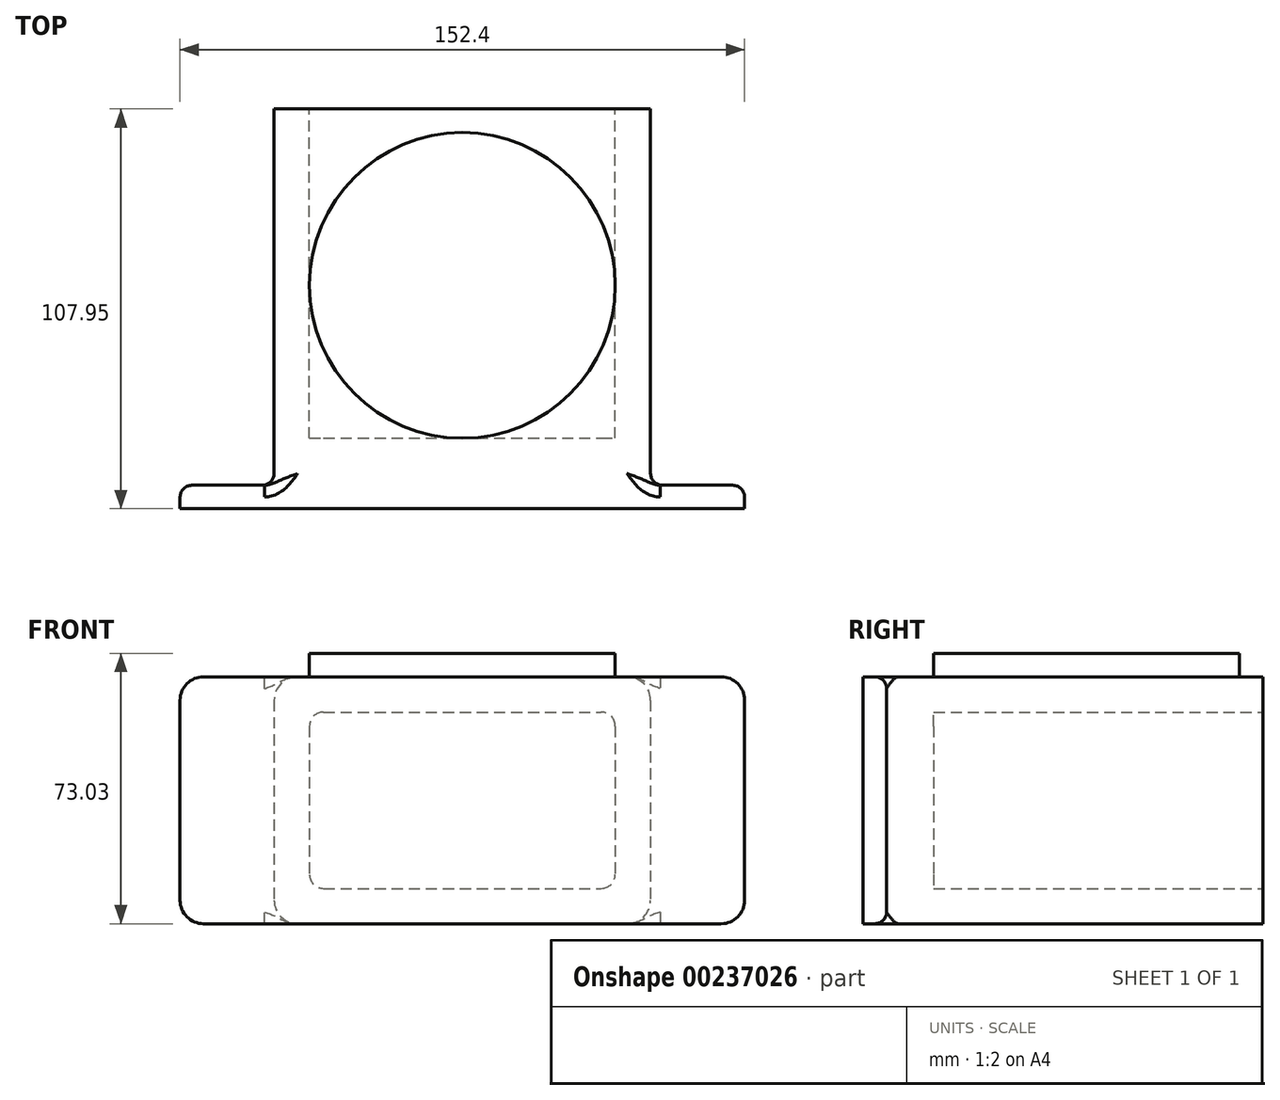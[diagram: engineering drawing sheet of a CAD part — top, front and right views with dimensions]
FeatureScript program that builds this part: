
annotation { "Feature Type Name" : "Feature", "Feature Type Description" : "" }
export const myFeature = defineFeature(function(context is Context, id is Id, definition is map)
    precondition{}
    {
        {
            var Q0;
            Q0=qCreatedBy(makeId("Front.planeOp"),FACE);
            var sketch = newSketch(context, id + "F0", { "sketchPlane" : qUnion([Q0])});
            skLineSegment(sketch, "E0.bottom", {"start": v(-76.2, -33.34) * mm, "end": v(76.2, -33.34) * mm});
            skLineSegment(sketch, "E0.top", {"start": v(-76.2, 33.34) * mm, "end": v(76.2, 33.34) * mm});
            skLineSegment(sketch, "E0.left", {"start": v(-76.2, -33.34) * mm, "end": v(-76.2, 33.34) * mm});
            skLineSegment(sketch, "E0.right", {"start": v(76.2, -33.34) * mm, "end": v(76.2, 33.34) * mm});
            skPoint(sketch, "E0.middle", {"position": v(0, 0) * mm});
            skSolve(sketch);
        }
        {
            var Q0;
            Q0=makeQuery(id+"F0.imprint","IMPRINT",FACE,{"disambiguationData":[TD([[makeQuery(id+"F0.imprint","IMPRINT",EDGE,{"derivedFrom":sQuery(id+"F0.wireOp",EDGE,"E0.bottom")}),1.0]])]});
            extrude(context, id + "F1", {"entities" : qUnion([Q0]), "depth" : 6.35 * mm});
        }
        {
            var Q0;
            Q0=makeQuery(id+"F1.opExtrude","CAP_FACE",FACE,{"disambiguationData":[OSD([sQuery(id+"F0.wireOp",EDGE,"E0.bottom"),sQuery(id+"F0.wireOp",EDGE,"E0.top"),sQuery(id+"F0.wireOp",EDGE,"E0.left"),sQuery(id+"F0.wireOp",EDGE,"E0.right")])],"isStart":true});
            var sketch = newSketch(context, id + "F2", { "sketchPlane" : qUnion([Q0])});
            skLineSegment(sketch, "E1.bottom", {"start": v(50.8, 33.34) * mm, "end": v(-50.8, 33.34) * mm});
            skLineSegment(sketch, "E1.top", {"start": v(50.8, -33.34) * mm, "end": v(-50.8, -33.34) * mm});
            skLineSegment(sketch, "E1.left", {"start": v(50.8, 33.34) * mm, "end": v(50.8, -33.34) * mm});
            skLineSegment(sketch, "E1.right", {"start": v(-50.8, 33.34) * mm, "end": v(-50.8, -33.34) * mm});
            skPoint(sketch, "E1.middle", {"position": v(0, 0) * mm});
            skSolve(sketch);
        }
        {
            var Q0;
            Q0=makeQuery(id+"F2.imprint","IMPRINT",FACE,{"disambiguationData":[TD([[makeQuery(id+"F2.imprint","IMPRINT",EDGE,{"derivedFrom":sQuery(id+"F2.wireOp",EDGE,"E1.bottom")}),1.0]])]});
            extrude(context, id + "F3", {"entities" : qUnion([Q0]), "operationType" : NewBodyOperationType.ADD, "depth" : 101.6 * mm});
        }
        {
            var Q0;
            Q0=makeQuery(id+"F3.opExtrude","SWEPT_EDGE",EDGE,{"disambiguationData":[OSD([sQuery(id+"F0.wireOp",EDGE,"E0.bottom"),sQuery(id+"F2.wireOp",EDGE,"E1.top"),sQuery(id+"F2.wireOp",EDGE,"E1.right")])]});
            var Q1;
            Q1=makeQuery(id+"F3.opExtrude","SWEPT_EDGE",EDGE,{"disambiguationData":[OSD([sQuery(id+"F0.wireOp",EDGE,"E0.top"),sQuery(id+"F2.wireOp",EDGE,"E1.bottom"),sQuery(id+"F2.wireOp",EDGE,"E1.right")])]});
            var Q2;
            Q2=makeQuery(id+"F3.opExtrude","SWEPT_EDGE",EDGE,{"disambiguationData":[OSD([sQuery(id+"F0.wireOp",EDGE,"E0.bottom"),sQuery(id+"F2.wireOp",EDGE,"E1.top"),sQuery(id+"F2.wireOp",EDGE,"E1.left")])]});
            var Q3;
            Q3=makeQuery(id+"F3.opExtrude","SWEPT_EDGE",EDGE,{"disambiguationData":[OSD([sQuery(id+"F0.wireOp",EDGE,"E0.top"),sQuery(id+"F2.wireOp",EDGE,"E1.bottom"),sQuery(id+"F2.wireOp",EDGE,"E1.left")])]});
            var Q4;
            Q4=makeQuery(id+"F1.opExtrude","SWEPT_EDGE",EDGE,{"disambiguationData":[OSD([sQuery(id+"F0.wireOp",EDGE,"E0.bottom"),sQuery(id+"F0.wireOp",EDGE,"E0.left")])]});
            var Q5;
            Q5=makeQuery(id+"F1.opExtrude","SWEPT_EDGE",EDGE,{"disambiguationData":[OSD([sQuery(id+"F0.wireOp",EDGE,"E0.top"),sQuery(id+"F0.wireOp",EDGE,"E0.left")])]});
            var Q6;
            Q6=makeQuery(id+"F1.opExtrude","SWEPT_EDGE",EDGE,{"disambiguationData":[OSD([sQuery(id+"F0.wireOp",EDGE,"E0.top"),sQuery(id+"F0.wireOp",EDGE,"E0.right")])]});
            var Q7;
            Q7=makeQuery(id+"F1.opExtrude","SWEPT_EDGE",EDGE,{"disambiguationData":[OSD([sQuery(id+"F0.wireOp",EDGE,"E0.bottom"),sQuery(id+"F0.wireOp",EDGE,"E0.right")])]});
            fillet(context, id + "F4", {"entities" : qUnion([Q0, Q1, Q2, Q3, Q4, Q5, Q6, Q7]), "radius" : 6.35 * mm, "tangentPropagation" : true, "allowEdgeOverflow" : false});
        }
        {
            var Q0;
            {var subQ0=sQuery(id+"F0.wireOp",EDGE,"E0.left");var subQ1=sQuery(id+"F0.wireOp",EDGE,"E0.top");var subQ2=sQuery(id+"F0.wireOp",EDGE,"E0.bottom");Q0=makeQuery(id+"F3.boolean.opBoolean","SPLIT",FACE,{"disambiguationData":[TD([makeQuery(id+"F1.opExtrude","SWEPT_FACE",FACE,{"disambiguationData":[OSD([subQ0])]})])],"derivedFrom":makeQuery(id+"F1.opExtrude","CAP_FACE",FACE,{"disambiguationData":[OSD([subQ2,subQ1,subQ0,sQuery(id+"F0.wireOp",EDGE,"E0.right")])],"isStart":true})});}
            var Q1;
            {var subQ0=sQuery(id+"F0.wireOp",EDGE,"E0.right");var subQ1=sQuery(id+"F0.wireOp",EDGE,"E0.top");var subQ2=sQuery(id+"F0.wireOp",EDGE,"E0.bottom");Q1=makeQuery(id+"F3.boolean.opBoolean","SPLIT",FACE,{"disambiguationData":[TD([makeQuery(id+"F1.opExtrude","SWEPT_FACE",FACE,{"disambiguationData":[OSD([subQ0])]})])],"derivedFrom":makeQuery(id+"F1.opExtrude","CAP_FACE",FACE,{"disambiguationData":[OSD([subQ2,subQ1,sQuery(id+"F0.wireOp",EDGE,"E0.left"),subQ0])],"isStart":true})});}
            fillet(context, id + "F5", {"entities" : qUnion([Q0, Q1]), "radius" : 3.17 * mm, "tangentPropagation" : true, "allowEdgeOverflow" : false});
        }
        {
            var Q0;
            Q0=makeQuery(id+"F3.opExtrude","CAP_FACE",FACE,{"disambiguationData":[OSD([sQuery(id+"F2.wireOp",EDGE,"E1.bottom"),sQuery(id+"F2.wireOp",EDGE,"E1.top"),sQuery(id+"F2.wireOp",EDGE,"E1.left"),sQuery(id+"F2.wireOp",EDGE,"E1.right")])],"isStart":false});
            var sketch = newSketch(context, id + "F6", { "sketchPlane" : qUnion([Q0])});
            skLineSegment(sketch, "E2.bottom", {"start": v(37.47, 23.81) * mm, "end": v(-37.46, 23.81) * mm});
            skLineSegment(sketch, "E2.top", {"start": v(37.47, -23.81) * mm, "end": v(-37.46, -23.81) * mm});
            skLineSegment(sketch, "E2.left", {"start": v(41.28, 20) * mm, "end": v(41.28, -20) * mm});
            skLineSegment(sketch, "E2.right", {"start": v(-41.27, 20) * mm, "end": v(-41.27, -20) * mm});
            skPoint(sketch, "E2.middle", {"position": v(0, 0) * mm});
            skPoint(sketch, "E3.visualSharp", {"position": v(-41.28, 23.81) * mm});
            skArc(sketch, "E3.filletArc", {"start": v(-37.46, 23.81) * mm, "mid": v(-40.16, 22.7) * mm, "end": v(-41.28, 20) * mm});
            skPoint(sketch, "E4.visualSharp", {"position": v(41.27, 23.81) * mm});
            skArc(sketch, "E4.filletArc", {"start": v(41.28, 20) * mm, "mid": v(40.16, 22.7) * mm, "end": v(37.47, 23.81) * mm});
            skPoint(sketch, "E5.visualSharp", {"position": v(41.27, -23.81) * mm});
            skArc(sketch, "E5.filletArc", {"start": v(37.47, -23.81) * mm, "mid": v(40.16, -22.7) * mm, "end": v(41.28, -20) * mm});
            skPoint(sketch, "E6.visualSharp", {"position": v(-41.28, -23.81) * mm});
            skArc(sketch, "E6.filletArc", {"start": v(-41.28, -20) * mm, "mid": v(-40.16, -22.7) * mm, "end": v(-37.46, -23.81) * mm});
            skSolve(sketch);
        }
        {
            var Q0;
            Q0=makeQuery(id+"F6.imprint","IMPRINT",FACE,{"disambiguationData":[TD([[makeQuery(id+"F6.imprint","IMPRINT",EDGE,{"derivedFrom":sQuery(id+"F6.wireOp",EDGE,"E2.bottom")}),1.0]])]});
            extrude(context, id + "F7", {"entities" : qUnion([Q0]), "operationType" : NewBodyOperationType.REMOVE, "oppositeDirection" : true, "depth" : 88.9 * mm});
        }
        {
            var Q0;
            Q0=makeQuery(id+"F3.boolean.opBoolean","MERGE",FACE,{"derivedFrom":[makeQuery(id+"F1.opExtrude","SWEPT_FACE",FACE,{"disambiguationData":[OSD([sQuery(id+"F0.wireOp",EDGE,"E0.top")])]}),makeQuery(id+"F3.opExtrude","SWEPT_FACE",FACE,{"disambiguationData":[OSD([sQuery(id+"F2.wireOp",EDGE,"E1.bottom")])]})]});
            var sketch = newSketch(context, id + "F8", { "sketchPlane" : qUnion([Q0])});
            skCircle(sketch, "E7", {"center": v(0, 53.98) * mm, "radius": 41.28 * mm});
            skSolve(sketch);
        }
        {
            var Q0;
            Q0=makeQuery(id+"F8.imprint","IMPRINT",FACE,{"disambiguationData":[TD([[makeQuery(id+"F8.imprint","IMPRINT",EDGE,{"derivedFrom":sQuery(id+"F8.wireOp",EDGE,"E7")}),1.0]])]});
            extrude(context, id + "F9", {"entities" : qUnion([Q0]), "operationType" : NewBodyOperationType.ADD, "depth" : 6.35 * mm});
        }
    });
